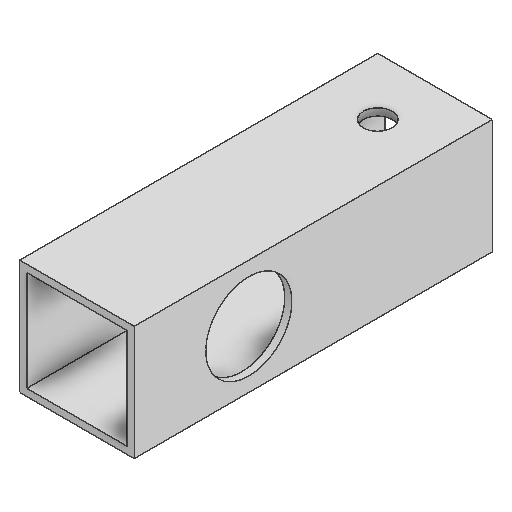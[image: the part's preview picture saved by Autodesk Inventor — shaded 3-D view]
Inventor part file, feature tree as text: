
AUTODESK INVENTOR PART (.ipt)
format: ipt  version: 2025.2 (Build 292293000, 293)  size: 136,192 bytes
history: native  units: in
note: dims shown in document units (in); Inventor stores cm internally (conversion verified against a paired STEP export)
features: extrude x3, sketch x3
ambient origin geometry x8: Origin, YZ Plane, XZ Plane, XY Plane, X Axis, Y Axis, Z Axis, Center Point
bodies: Solid1 (feature_tree)
feature tree (6):
  extrude  "Extrusion1"  Depth=1.0in
  extrude  "Extrusion2"  Depth=0.0625in
  extrude  "Extrusion3"  Depth=0.0625in
  sketch  "Sketch1"  dims[d0=1.0in d1=1.0in]
  sketch  "Sketch2"  dims[d2=0.0625in d3=0.0625in]
  sketch  "Sketch3"  dims[d4=0.0625in d5=0.0625in d6=3.125in d7=0.0in d8=0.75in d9=0.0in d10=0.0in d11=0.5in d12=1.0in d13=0.8in d14=0.25in d15=0.25in d16=0.8in d17=0.25in d18=0.5in d19=0.5in d20=0.0in d21=0.0in]
